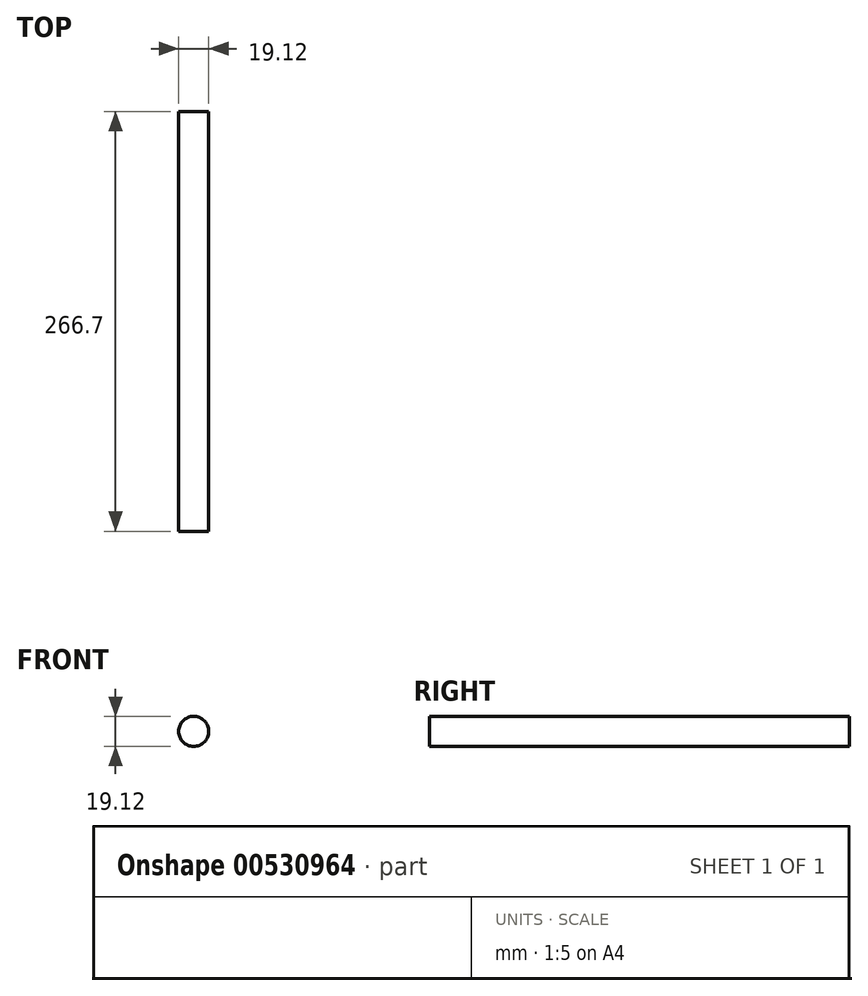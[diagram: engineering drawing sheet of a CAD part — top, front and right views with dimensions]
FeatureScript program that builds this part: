
annotation { "Feature Type Name" : "Feature", "Feature Type Description" : "" }
export const myFeature = defineFeature(function(context is Context, id is Id, definition is map)
    precondition{}
    {
        {
            var Q0;
            Q0=qCreatedBy(makeId("Front.planeOp"),FACE);
            var sketch = newSketch(context, id + "F0", { "sketchPlane" : qUnion([Q0])});
            skCircle(sketch, "E0", {"center": v(0, 0) * mm, "radius": 9.56 * mm});
            skCircle(sketch, "E1", {"center": v(0, 0) * mm, "radius": 8.33 * mm});
            skSolve(sketch);
        }
        {
            var Q0;
            Q0 = qSketchRegion(id + "F0", true);
            var Q1;
            Q1=makeQuery(id+"F0.imprint","IMPRINT",FACE,{"disambiguationData":[TD([[makeQuery(id+"F0.imprint","IMPRINT",EDGE,{"derivedFrom":sQuery(id+"F0.wireOp",EDGE,"E1")}),1.0]])]});
            extrude(context, id + "F1", {"entities" : qUnion([Q0, Q1]), "depth" : 266.7 * mm, "offsetDistance" : 25.4 * mm});
        }
    });
